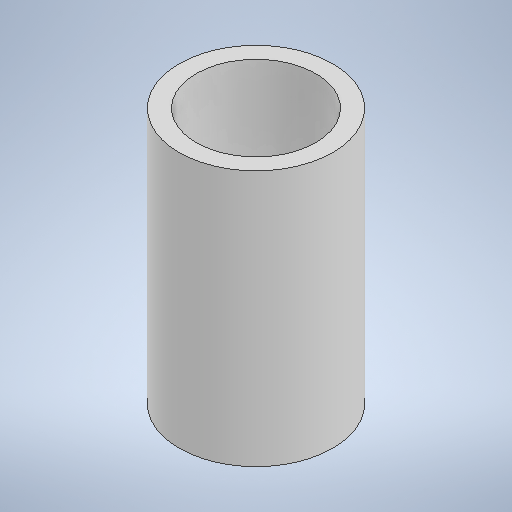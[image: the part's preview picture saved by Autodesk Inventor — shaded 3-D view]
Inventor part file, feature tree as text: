
AUTODESK INVENTOR PART (.ipt)
format: ipt  version: 2025.1 (Build 291241000, 241)  size: 258,048 bytes
history: native  units: mm
features: extrude x1, sketch x1
ambient origin geometry x8: Origin, YZ Plane, XZ Plane, XY Plane, X Axis, Y Axis, Z Axis, Center Point
bodies: Solid1 (feature_tree)
feature tree (2):
  extrude  "Extrusion1"  Depth=15.0mm
  sketch  "Sketch1"  dims[d0=9.0mm d1=7.0mm d2=15.0mm d3=0.0mm]
